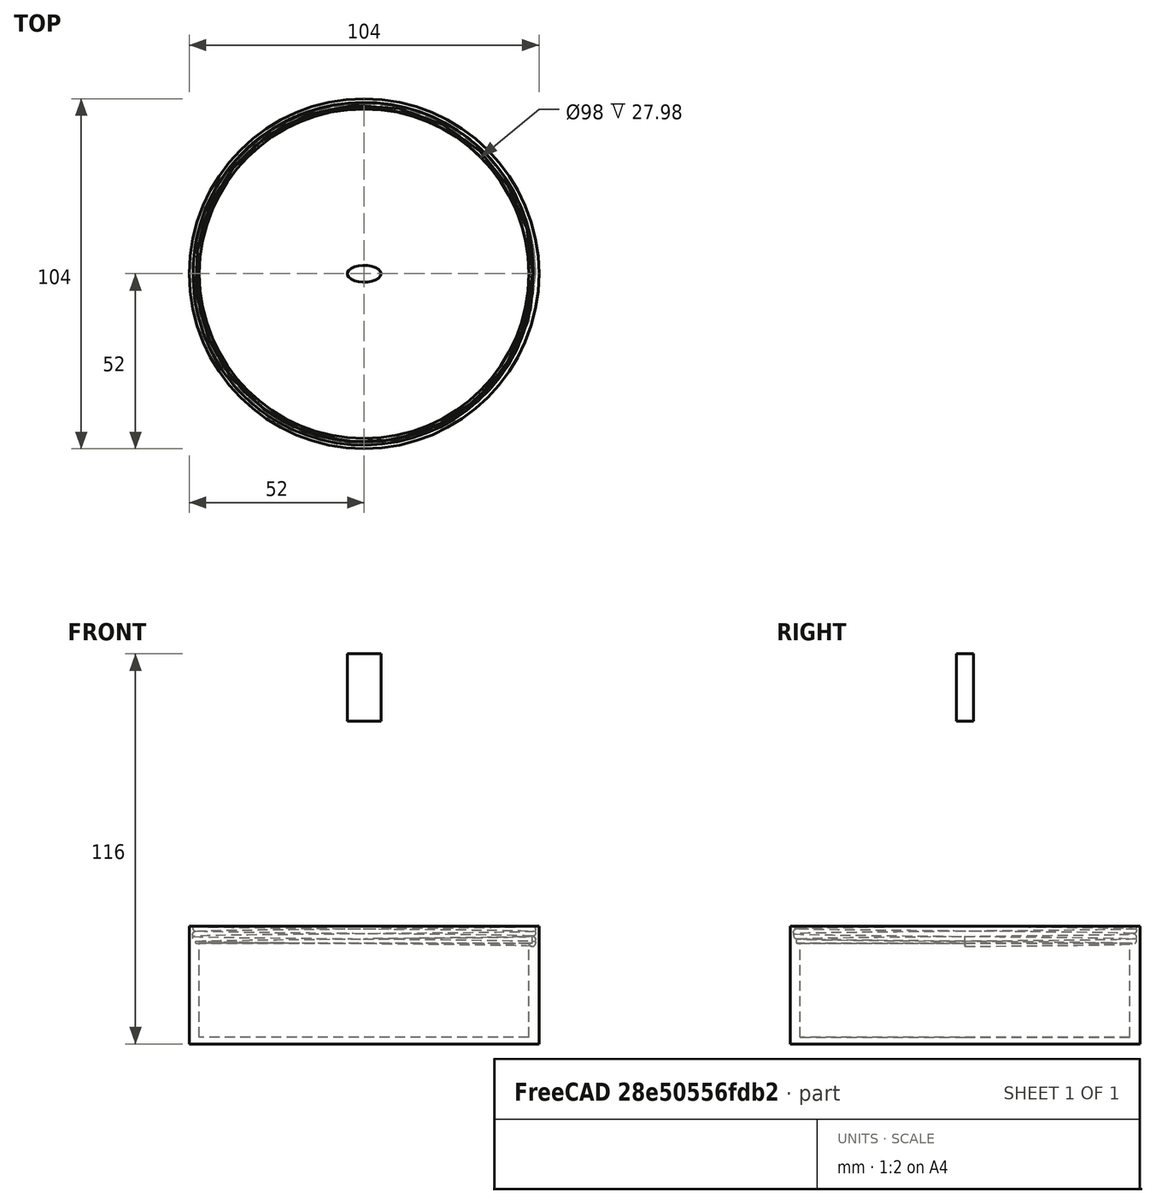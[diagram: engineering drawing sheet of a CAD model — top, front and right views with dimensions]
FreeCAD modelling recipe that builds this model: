
FCSTD DOCUMENT  (FreeCAD 0.17R13522 (Git))
Label: tuna_wringer_bottom
License: CreativeCommons Attribution-ShareAlike
LicenseURL: http://creativecommons.org/licenses/by-sa/4.0/
objects: Part::Cut×22, Part::Feature×15, Part::Cylinder×9, Part::MultiFuse×5, Part::Box×4, Sketcher::SketchObject×4, Part::Extrusion×3, Part::Sweep×3, PartDesign::Body×2, Part::Helix×2, Part::Ellipse×1, Part::FeaturePython×1, Part::MultiCommon×1, PartDesign::ShapeBinder×1, App::DocumentObjectGroup×1
note: 73 computed .brp shape members not serialized (recipe doc carries the construction recipe); baked Part::Feature solids carry a one-line shape summary decoded from their .brp

FEATURE [Part::Cylinder] Cylinder001  label="base_parte_inferior"
  Angle = 360
  AttacherType = Attacher::AttachEngine3D
  Height = 35
  Placement = pos=(0,0,-30) rot=(0,0,1;0rad)
  Radius = 52
FEATURE [Part::Feature] Fusion001  label="base_roscada_media_para_roscar_recipiente_inferior"
  shape: bbox 110.9 x 119.3 x 43.76 mm, 46 faces (baked)
FEATURE [Part::Cut] Cut
  Base = -> Cylinder001
  Tool = -> Fusion001
FEATURE [Part::Cylinder] Cylinder002  label="perforador_parte_inferior"
  Angle = 360
  AttacherType = Attacher::AttachEngine3D
  Height = 29
  Placement = pos=(0,0,-28) rot=(0,0,1;0rad)
  Radius = 49
FEATURE [Part::Feature] Fusion002  label="base_roscada_media001"
  shape: bbox 110.9 x 119.3 x 43.76 mm, 46 faces (baked)
FEATURE [Part::Cylinder] Cylinder003  label="Cylinder001"
  Angle = 360
  AttacherType = Attacher::AttachEngine3D
  Height = 40
  Placement = pos=(0,0,5) rot=(0,0,1;0rad)
  Radius = 52
FEATURE [Part::MultiFuse] Fusion003  label="parte_media_comienzo"
  Shapes = -> [Fusion002,Cylinder003]
FEATURE [Part::Feature] Fusion004  label="base_roscada_media002"
  Placement = pos=(0,0,8) rot=(0,0,1;0rad)
  shape: bbox 110.9 x 119.3 x 43.76 mm, 46 faces (baked)
FEATURE [Part::Cut] Cut002  label="parte_media_2"
  Base = -> Fusion003
  Tool = -> Fusion004
FEATURE [Part::Cylinder] Cylinder004  label="Cylinder002"
  Angle = 360
  AttacherType = Attacher::AttachEngine3D
  Height = 10
  Placement = pos=(0,0,-10) rot=(0,0,1;0rad)
  Radius = 60
FEATURE [Part::Cut] Cut003  label="parte_media_sin_perforar"
  Base = -> Cut002
  Tool = -> Cylinder004
FEATURE [Part::Feature] Fusion005  label="tapa_rosca"
  shape: bbox 110.9 x 119.3 x 43.76 mm, 46 faces (baked)
FEATURE [Part::Cylinder] Cylinder005  label="Cylinder003"
  Angle = 360
  AttacherType = Attacher::AttachEngine3D
  Height = 40
  Placement = pos=(0,0,4) rot=(0,0,1;0rad)
  Radius = 54
FEATURE [Part::Cut] Cut004
  Base = -> Fusion005
  Tool = -> Cylinder005
FEATURE [Part::Cylinder] Cylinder006  label="Cylinder004"
  Angle = 360
  AttacherType = Attacher::AttachEngine3D
  Height = 1
  Placement = pos=(0,0,4) rot=(0,0,1;0rad)
  Radius = 50
FEATURE [Part::MultiFuse] Fusion006
  Shapes = -> [Cut004,Cylinder006]
FEATURE [Part::Ellipse] Ellipse
  Angle0 = 0
  Angle1 = 360
  AttacherType = Attacher::AttachEngine3D
  MajorRadius = 5
  MinorRadius = 2.5
FEATURE [Part::Extrusion] Extrude
  Base = -> Ellipse
  Dir = (0,0,1)
  DirMode = 2
  FaceMakerClass = Part::FaceMakerBullseye
  LengthFwd = 20
  LengthRev = 0
  Solid = true
  Symmetric = false
FEATURE [Part::Extrusion] Extrude001
  Base = -> Ellipse
  Dir = (0,0,1)
  DirMode = 2
  FaceMakerClass = Part::FaceMakerBullseye
  LengthFwd = 20
  LengthRev = 0
  Solid = true
  Symmetric = false
FEATURE [Part::Extrusion] Extrude002
  Base = -> Ellipse
  Dir = (0,0,1)
  DirMode = 2
  FaceMakerClass = Part::FaceMakerBullseye
  LengthFwd = 20
  LengthRev = 0
  Solid = true
  Symmetric = false
FEATURE [Part::FeaturePython] Array  # Draft array (typed FeaturePython)
  Angle = 360
  ArrayType = 0
  Axis = (0,0,1)
  Base = -> Extrude
  Center = (0,0,0)
  Fuse = false
  IntervalAxis = (0,0,0)
  IntervalX = (14,0,0)
  IntervalY = (0,9,0)
  IntervalZ = (0,0,0)
  NumberPolar = 1
  NumberX = 30
  NumberY = 30
  NumberZ = 1
FEATURE [Part::Cylinder] Cylinder007  label="Cylinder005"
  Angle = 360
  AttacherType = Attacher::AttachEngine3D
  Height = 50
  Placement = pos=(77,135,-2) rot=(0,0,1;0rad)
  Radius = 48
FEATURE [Part::MultiCommon] Common
  Placement = pos=(39,-136,0) rot=(0,0,1;0rad)
  Shapes = -> [Array,Cylinder007]
FEATURE [Part::Box] Box  label="Cube"
  AttacherType = Attacher::AttachEngine3D
  Height = 60
  Length = 10
  Placement = pos=(92,40,-5) rot=(0,0,1;0rad)
  Width = 10
FEATURE [Part::Feature] Box001  label="Cube001"
  Placement = pos=(132,40,-5) rot=(0,0,1;0rad)
  shape: bbox 10 x 10 x 60 mm, 6 faces (baked)
FEATURE [Part::Feature] Box001001  label="Cube002"
  Placement = pos=(146,30,-5) rot=(0,0,1;0rad)
  shape: bbox 10 x 10 x 60 mm, 6 faces (baked)
FEATURE [Part::Feature] Box001001001  label="Cube003"
  Placement = pos=(77,30,-5) rot=(0,0,1;0rad)
  shape: bbox 10 x 10 x 60 mm, 6 faces (baked)
FEATURE [Part::Feature] Box001001001001  label="Cube004"
  Placement = pos=(77,-43,-5) rot=(0,0,1;0rad)
  shape: bbox 10 x 10 x 60 mm, 6 faces (baked)
FEATURE [Part::Feature] Box001001001001001  label="Cube005"
  Placement = pos=(146,-43,-5) rot=(0,0,1;0rad)
  shape: bbox 10 x 10 x 60 mm, 6 faces (baked)
FEATURE [Part::Feature] Box001001001001001001  label="Cube006"
  Placement = pos=(130,-52,-5) rot=(0,0,1;0rad)
  shape: bbox 10 x 10 x 60 mm, 6 faces (baked)
FEATURE [Part::Feature] Box001001001001001001001  label="Cube007"
  Placement = pos=(91,-52,-5) rot=(0,0,1;0rad)
  shape: bbox 10 x 10 x 60 mm, 6 faces (baked)
FEATURE [Part::Feature] Box001001001001001001002  label="Cube008"
  Placement = pos=(64,13,-5) rot=(0,0,1;0rad)
  shape: bbox 10 x 10 x 60 mm, 6 faces (baked)
FEATURE [Part::Feature] Box001001001001001001002001  label="Cube009"
  Placement = pos=(64,-25,-5) rot=(0,0,1;0rad)
  shape: bbox 10 x 10 x 60 mm, 6 faces (baked)
FEATURE [Part::Feature] Box001001001001001001002001001  label="Cube010"
  Placement = pos=(159,-25,-5) rot=(0,0,1;0rad)
  shape: bbox 10 x 10 x 60 mm, 6 faces (baked)
FEATURE [Part::Feature] Box001001001001001001002001001001  label="Cube011"
  Placement = pos=(159,12,-5) rot=(0,0,1;0rad)
  shape: bbox 10 x 10 x 60 mm, 6 faces (baked)
FEATURE [Part::Cut] Cut005
  Base = -> Common
  Tool = -> Box
FEATURE [Part::Cut] Cut006
  Base = -> Cut005
  Tool = -> Box001
FEATURE [Part::Cut] Cut007
  Base = -> Cut006
  Tool = -> Box001001
FEATURE [Part::Cut] Cut008
  Base = -> Cut007
  Tool = -> Box001001001
FEATURE [Part::Cut] Cut009
  Base = -> Cut008
  Tool = -> Box001001001001
FEATURE [Part::Cut] Cut010
  Base = -> Cut009
  Tool = -> Box001001001001001
FEATURE [Part::Cut] Cut011
  Base = -> Cut010
  Tool = -> Box001001001001001001
FEATURE [Part::Cut] Cut012
  Base = -> Cut011
  Tool = -> Box001001001001001001001
FEATURE [Part::Cut] Cut013
  Base = -> Cut012
  Tool = -> Box001001001001001001002
FEATURE [Part::Cut] Cut014
  Base = -> Cut013
  Tool = -> Box001001001001001001002001
FEATURE [Part::Cut] Cut015
  Base = -> Cut014
  Tool = -> Box001001001001001001002001001
FEATURE [Part::Cut] Cut016  label="rejilla"
  Base = -> Cut015
  Placement = pos=(-116,1,-9) rot=(0,0,1;0rad)
  Tool = -> Box001001001001001001002001001001
FEATURE [Part::Cut] Cut017  label="parte_media"
  Base = -> Cut003
  Tool = -> Cut016
FEATURE [Part::Box] Box001001001001001001002001001002  label="Cube012"
  AttacherType = Attacher::AttachEngine3D
  Height = 200
  Length = 200
  Placement = pos=(-89,-91,-6) rot=(0,0,1;0rad)
  Width = 200
FEATURE [Sketcher::SketchObject] Sketch001
  Placement = pos=(0,0,0) rot=(1,0,0;1.5708rad)
  sketch-geometry (1):
    g0: ArcOfCircle CenterX=0 CenterY=0 CenterZ=0 NormalX=0 NormalY=0 NormalZ=1 AngleXU=0 Radius=30.8415 StartAngle=0.00522177 EndAngle=3.12837
  constraints (1):
    c: Coincident(g0,g-1)
FEATURE [Part::Cut] Cut001  label="parte_inferior_done"
  Base = -> Cut
  Placement = pos=(0,0,-66) rot=(0,0,1;0rad)
  Tool = -> Cylinder002
FEATURE [Part::Cylinder] Cylinder
  Angle = 360
  AttacherType = Attacher::AttachEngine3D
  Height = 40
  Radius = 50
FEATURE [Sketcher::SketchObject] Sketch
  MapMode = 5
  Placement = pos=(0,0,0) rot=(1,0,0;1.5708rad)
  Support = -> [XZ_Plane]
  sketch-geometry (1):
    g0: Circle CenterX=50 CenterY=0 CenterZ=0 NormalX=0 NormalY=0 NormalZ=1 AngleXU=0 Radius=1
  constraints (3):
    c: PointOnObject(g0,g-1)
    c: Radius(g0) = 1
    c: DistanceX(g-1,g0) = 50
FEATURE [PartDesign::ShapeBinder] CopyFusion006
  Placement = pos=(0,0,4) rot=(0,0,1;0rad)
FEATURE [PartDesign::Body] Body
  Group = -> [Sketch,CopyFusion006]
  Origin = -> Origin
FEATURE [Part::Helix] Helix
  Angle = 0
  AttacherType = Attacher::AttachEngine3D
  Height = 40
  LocalCoord = 0
  Pitch = 3
  Radius = 50
  Style = 1
FEATURE [Part::Sweep] Sweep
  Frenet = false
  Sections = -> [Sketch]
  Solid = true
  Spine = -> Helix
  Transition = 1
FEATURE [Part::MultiFuse] Fusion  label="base_roscada_media"
  Shapes = -> [Sweep,Cylinder]
FEATURE [Part::Box] Box001001001001001001002001001003  label="Cube013"
  AttacherType = Attacher::AttachEngine3D
  Height = 200
  Length = 200
  Placement = pos=(-89,-91,-6) rot=(0,0,1;0rad)
  Width = 200
FEATURE [Part::Cut] Cut018
  Base = -> Cut017
  Tool = -> Box001001001001001001002001001002
FEATURE [Sketcher::SketchObject] Sketch002
  Placement = pos=(0,0,5) rot=(0,0,1;0rad)
  sketch-geometry (1):
    g0: Circle CenterX=30 CenterY=0 CenterZ=0 NormalX=0 NormalY=0 NormalZ=1 AngleXU=0 Radius=7.5
  constraints (3):
    c: PointOnObject(g0,g-1)
    c: Radius(g0) = 7.5
    c: DistanceX(g-1,g0) = 30
FEATURE [Part::Sweep] Sweep001  label="manija"
  Frenet = false
  Placement = pos=(0,0,4) rot=(0,0,1;0rad)
  Sections = -> [Sketch002]
  Solid = true
  Spine = -> Sketch001
  Transition = 1
FEATURE [Part::MultiFuse] Fusion007  label="tapa_con_rosca"
  Placement = pos=(0,0,104) rot=(0,0,1;0rad)
  Shapes = -> [Fusion006,Sweep001]
FEATURE [Part::Cut] Cut019
  Base = -> Fusion007
  Tool = -> Box001001001001001001002001001003
FEATURE [Part::Box] Box001001001001001001002001001004  label="Cube014"
  AttacherType = Attacher::AttachEngine3D
  Height = 200
  Length = 200
  Placement = pos=(-89,-91,-6) rot=(0,0,1;0rad)
  Width = 200
FEATURE [Part::Cut] Cut020
  Base = -> Fusion
  Tool = -> Box001001001001001001002001001004
FEATURE [App::DocumentObjectGroup] Group  label="not used"
  Group = -> [Body,Helix,Cut018,Cut019,Cut020,Extrude001,Extrude002,Sketch001]
FEATURE [Part::Helix] Helix001
  Angle = 0
  AttacherType = Attacher::AttachEngine3D
  Height = 40
  LocalCoord = 0
  Pitch = 3
  Radius = 50
  Style = 1
FEATURE [Sketcher::SketchObject] Sketch003
  MapMode = 5
  Placement = pos=(0,0,0) rot=(1,0,0;1.5708rad)
  Support = -> [XZ_Plane001]
  sketch-geometry (1):
    g0: Circle CenterX=50 CenterY=0.004902 CenterZ=0 NormalX=0 NormalY=0 NormalZ=1 AngleXU=0 Radius=1.02
  constraints (2):
    c: Radius(g0) = 1.02
    c: DistanceX(g-1,g0) = 50
FEATURE [PartDesign::Body] Body001
  Group = -> [Sketch003]
  Origin = -> Origin001
FEATURE [Part::Cylinder] Cylinder008  label="Cylinder006"
  Angle = 360
  AttacherType = Attacher::AttachEngine3D
  Height = 60
  Placement = pos=(0,0,-1.02) rot=(0,0,1;0rad)
  Radius = 50
FEATURE [Part::Sweep] Sweep002
  Frenet = false
  Sections = -> [Sketch003]
  Solid = true
  Spine = -> Helix001
  Transition = 1
FEATURE [Part::MultiFuse] Fusion008
  Placement = pos=(0,0,-65) rot=(0,0,1;0rad)
  Shapes = -> [Sweep002,Cylinder008]
FEATURE [Part::Cut] Cut021
  Base = -> Cut001
  Tool = -> Fusion008
